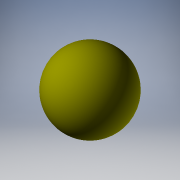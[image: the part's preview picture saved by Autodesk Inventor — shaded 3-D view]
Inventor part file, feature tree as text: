
AUTODESK INVENTOR PART (.ipt)
format: ipt  version: 2019 (Build 230136000, 136)  size: 141,312 bytes
history: native  units: mm
features: revolve x1, sketch x1
ambient origin geometry x8: Origin, YZ Plane, XZ Plane, XY Plane, X Axis, Y Axis, Z Axis, Center Point
bodies: Solid1 (feature_tree)
feature tree (2):
  revolve  "Revolution1"  [1 undecoded]
  sketch  "Sketch_6"  dims[d0=360.0deg]
note: 1 required parameter value undecoded (feature->parameter linkage not recoverable at this tier; creation-order binding heuristic only, values carry confidence <= 0.55)
